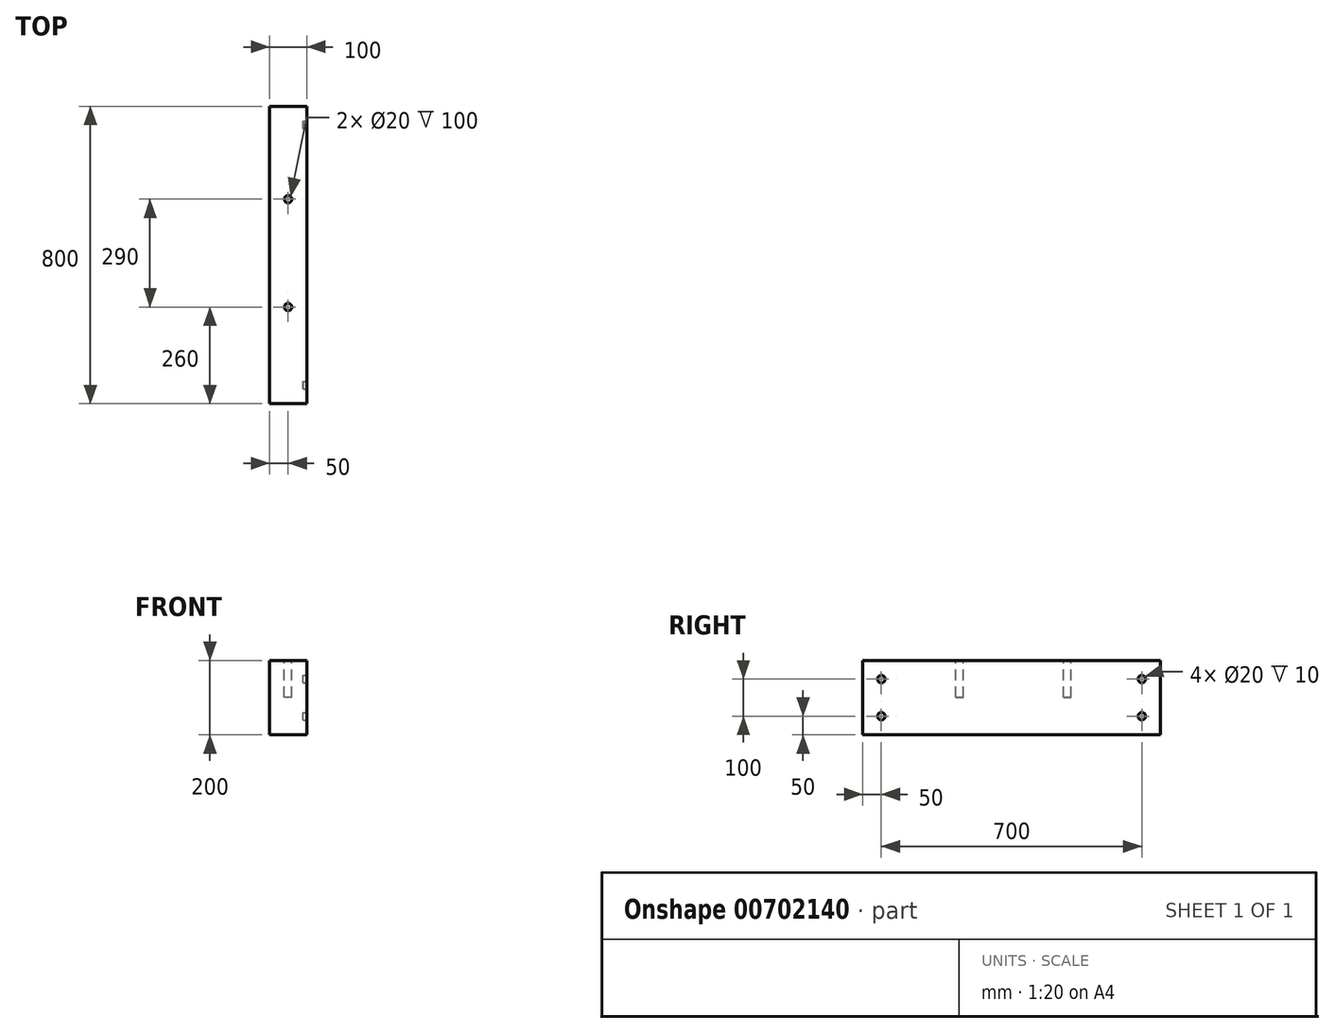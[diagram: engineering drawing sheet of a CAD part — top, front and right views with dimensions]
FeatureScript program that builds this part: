
annotation { "Feature Type Name" : "Feature", "Feature Type Description" : "" }
export const myFeature = defineFeature(function(context is Context, id is Id, definition is map)
    precondition{}
    {
        {
            var Q0;
            Q0=qCreatedBy(makeId("Front.planeOp"),FACE);
            var sketch = newSketch(context, id + "F0", { "sketchPlane" : qUnion([Q0])});
            skLineSegment(sketch, "E0.bottom", {"start": v(0, 0) * mm, "end": v(-100, 0) * mm});
            skLineSegment(sketch, "E0.top", {"start": v(0, 200) * mm, "end": v(-100, 200) * mm});
            skLineSegment(sketch, "E0.left", {"start": v(0, 0) * mm, "end": v(0, 200) * mm});
            skLineSegment(sketch, "E0.right", {"start": v(-100, 0) * mm, "end": v(-100, 200) * mm});
            skSolve(sketch);
        }
        {
            var Q0;
            Q0=qSketchRegion(id+"F0",true);
            extrude(context, id + "F1", {"entities" : qUnion([Q0]), "depth" : 800 * mm, "offsetDistance" : 25 * mm});
        }
        {
            var Q0;
            Q0=makeQuery(id+"F1.opExtrude","SWEPT_FACE",FACE,{"disambiguationData":[OSD([sQuery(id+"F0.wireOp",EDGE,"E0.left")])]});
            var sketch = newSketch(context, id + "F2", { "sketchPlane" : qUnion([Q0])});
            skCircle(sketch, "E1", {"center": v(-750, 150) * mm, "radius": 10 * mm});
            skCircle(sketch, "E2", {"center": v(-750, 50) * mm, "radius": 10 * mm});
            skCircle(sketch, "E3", {"center": v(-50, 150) * mm, "radius": 10 * mm});
            skCircle(sketch, "E4", {"center": v(-50, 50) * mm, "radius": 10 * mm});
            skSolve(sketch);
        }
        {
            var Q0;
            Q0=qSketchRegion(id+"F2",true);
            extrude(context, id + "F3", {"entities" : qUnion([Q0]), "operationType" : NewBodyOperationType.REMOVE, "oppositeDirection" : true, "depth" : 10 * mm, "offsetDistance" : 25 * mm});
        }
        {
            var Q0;
            Q0=makeQuery(id+"F1.opExtrude","SWEPT_FACE",FACE,{"disambiguationData":[OSD([sQuery(id+"F0.wireOp",EDGE,"E0.top")])]});
            var sketch = newSketch(context, id + "F4", { "sketchPlane" : qUnion([Q0])});
            skCircle(sketch, "E5", {"center": v(-50, -250) * mm, "radius": 10 * mm});
            skPoint(sketch, "E5.centerSnap0", {"position": v(-50, 0) * mm});
            skCircle(sketch, "E6", {"center": v(-50, -540) * mm, "radius": 10 * mm});
            skPoint(sketch, "E6.centerSnap0", {"position": v(-50, -800) * mm});
            skSolve(sketch);
        }
        {
            var Q0;
            Q0=qSketchRegion(id+"F4",true);
            extrude(context, id + "F5", {"entities" : qUnion([Q0]), "operationType" : NewBodyOperationType.REMOVE, "oppositeDirection" : true, "depth" : 100 * mm, "offsetDistance" : 25 * mm});
        }
    });
